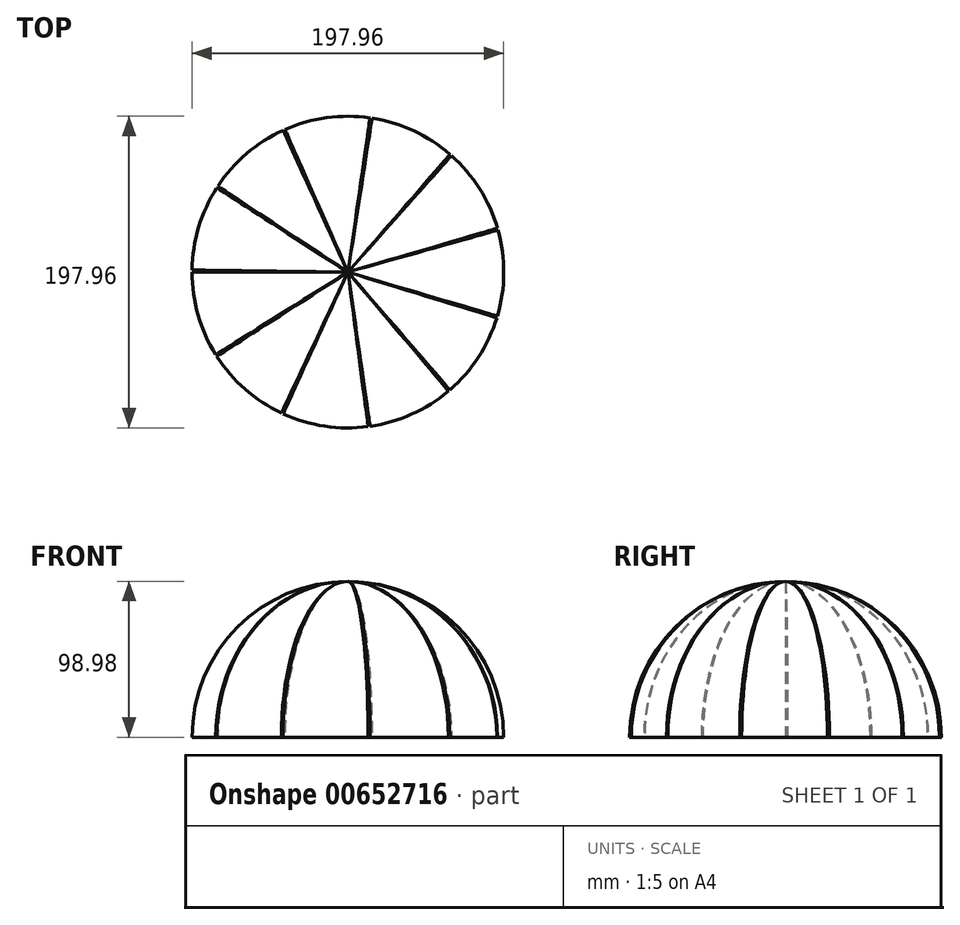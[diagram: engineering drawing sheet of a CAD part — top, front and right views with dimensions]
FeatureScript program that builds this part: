
annotation { "Feature Type Name" : "Feature", "Feature Type Description" : "" }
export const myFeature = defineFeature(function(context is Context, id is Id, definition is map)
    precondition{}
    {
        {
            var Q0;
            Q0=qCreatedBy(makeId("Front.planeOp"),FACE);
            var sketch = newSketch(context, id + "F0", { "sketchPlane" : qUnion([Q0])});
            skLineSegment(sketch, "E0", {"start": v(0, -69.87) * mm, "end": v(0, 68.05) * mm, "construction": true});
            skSolve(sketch);
        }
        {
            var Q0;
            Q0=qCreatedBy(makeId("Front.planeOp"),FACE);
            var sketch = newSketch(context, id + "F1", { "sketchPlane" : qUnion([Q0])});
            skArc(sketch, "E1", {"start": v(0, 98.68) * mm, "mid": v(-69.77, 69.77) * mm, "end": v(-98.68, 0) * mm});
            skArc(sketch, "E2", {"start": v(-98.98, 0) * mm, "mid": v(-69.99, 69.99) * mm, "end": v(0, 98.98) * mm});
            skLineSegment(sketch, "E3", {"start": v(-98.98, 0) * mm, "end": v(-98.68, 0) * mm});
            skLineSegment(sketch, "E4", {"start": v(0, 98.98) * mm, "end": v(0, 98.68) * mm});
            skSolve(sketch);
        }
        {
            var Q0;
            Q0=qCreatedBy(makeId("Front.planeOp"),FACE);
            var sketch = newSketch(context, id + "F2", { "sketchPlane" : qUnion([Q0])});
            skLineSegment(sketch, "E5", {"start": v(0, 70.26) * mm, "end": v(0, -60.77) * mm, "construction": true});
            skSolve(sketch);
        }
        {
            var Q0;
            Q0=sQuery(id+"F1.wireOp",EDGE,"E2");
            var Q1;
            Q1=sQuery(id+"F0.wireOp",EDGE,"E0");
            revolve(context, id + "F3", {"bodyType" : ToolBodyType.SURFACE, "surfaceEntities" : qUnion([Q0]), "axis" : qUnion([Q1]), "revolveType" : RevolveType.ONE_DIRECTION, "angle" : 32 * degree});
        }
        {
            var Q0;
            Q0=makeQuery(id+"F3.opRevolve","SWEPT_BODY",BODY,{"disambiguationData":[OSD([sQuery(id+"F1.wireOp",EDGE,"E2")])]});
            var Q1;
            Q1=sQuery(id+"F2.wireOp",EDGE,"E5");
            circularPattern(context, id + "F4", {"entities" : qUnion([Q0]), "axis" : qUnion([Q1]), "angle" : 360 * degree, "instanceCount" : 11, "equalSpace" : true});
        }
    });
